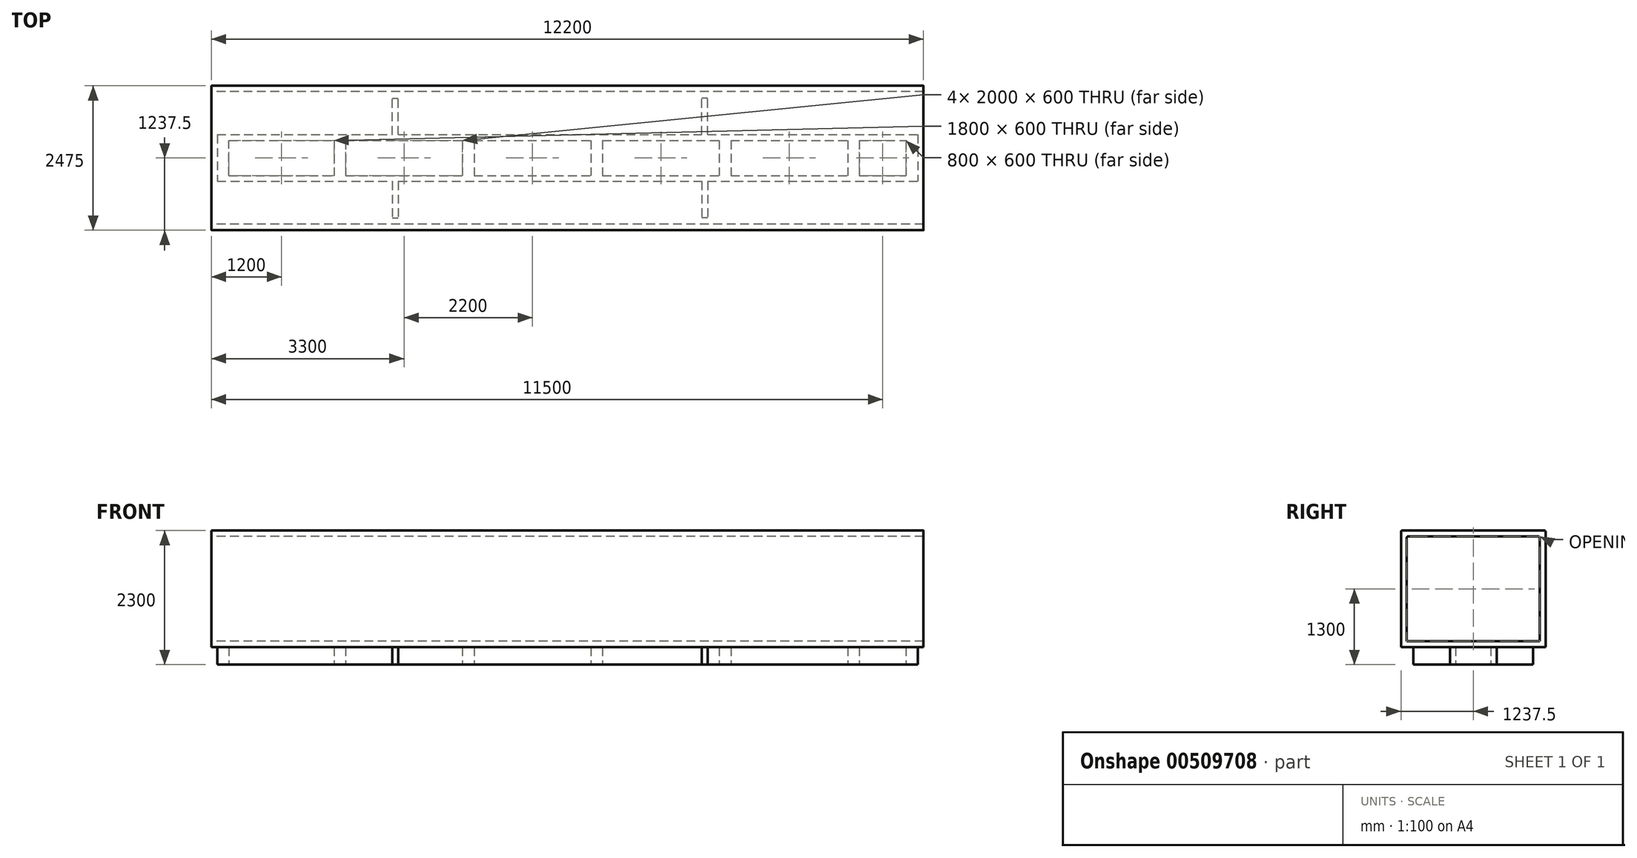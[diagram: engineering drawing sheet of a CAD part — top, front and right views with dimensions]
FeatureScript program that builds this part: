
annotation { "Feature Type Name" : "Feature", "Feature Type Description" : "" }
export const myFeature = defineFeature(function(context is Context, id is Id, definition is map)
    precondition{}
    {
        {
            var Q0;
            Q0=qCreatedBy(makeId("Top.planeOp"),FACE);
            var sketch = newSketch(context, id + "F0", { "sketchPlane" : qUnion([Q0])});
            skLineSegment(sketch, "E0.bottom", {"start": v(-69.8, 600) * mm, "end": v(11930.2, 600) * mm});
            skLineSegment(sketch, "E0.top", {"start": v(-69.8, 0) * mm, "end": v(11930.2, 0) * mm});
            skLineSegment(sketch, "E0.left", {"start": v(-69.8, 600) * mm, "end": v(-69.8, 0) * mm});
            skLineSegment(sketch, "E0.right", {"start": v(11930.2, 600) * mm, "end": v(11930.2, 0) * mm});
            skLineSegment(sketch, "E1.bottom", {"start": v(1930.2, 600) * mm, "end": v(2130.2, 600) * mm});
            skLineSegment(sketch, "E1.top", {"start": v(1930.2, 0) * mm, "end": v(2130.2, 0) * mm});
            skLineSegment(sketch, "E1.left", {"start": v(1930.2, 600) * mm, "end": v(1930.2, 0) * mm});
            skLineSegment(sketch, "E1.right", {"start": v(2130.2, 600) * mm, "end": v(2130.2, 0) * mm});
            skLineSegment(sketch, "E2.bottom", {"start": v(4130.2, 600) * mm, "end": v(4330.2, 600) * mm});
            skLineSegment(sketch, "E2.top", {"start": v(4130.2, 0) * mm, "end": v(4330.2, 0) * mm});
            skLineSegment(sketch, "E2.left", {"start": v(4130.2, 600) * mm, "end": v(4130.2, 0) * mm});
            skLineSegment(sketch, "E2.right", {"start": v(4330.2, 600) * mm, "end": v(4330.2, 0) * mm});
            skLineSegment(sketch, "E3.bottom", {"start": v(6330.2, 600) * mm, "end": v(6530.2, 600) * mm});
            skLineSegment(sketch, "E3.top", {"start": v(6330.2, 0) * mm, "end": v(6530.2, 0) * mm});
            skLineSegment(sketch, "E3.left", {"start": v(6330.2, 600) * mm, "end": v(6330.2, 0) * mm});
            skLineSegment(sketch, "E3.right", {"start": v(6530.2, 600) * mm, "end": v(6530.2, 0) * mm});
            skLineSegment(sketch, "E4.bottom", {"start": v(8530.2, 600) * mm, "end": v(8730.2, 600) * mm});
            skLineSegment(sketch, "E4.top", {"start": v(8530.2, 0) * mm, "end": v(8730.2, 0) * mm});
            skLineSegment(sketch, "E4.left", {"start": v(8530.2, 600) * mm, "end": v(8530.2, 0) * mm});
            skLineSegment(sketch, "E4.right", {"start": v(8730.2, 600) * mm, "end": v(8730.2, 0) * mm});
            skLineSegment(sketch, "E5.bottom", {"start": v(10730.2, 600) * mm, "end": v(10930.2, 600) * mm});
            skLineSegment(sketch, "E5.top", {"start": v(10730.2, 0) * mm, "end": v(10930.2, 0) * mm});
            skLineSegment(sketch, "E5.left", {"start": v(10730.2, 600) * mm, "end": v(10730.2, 0) * mm});
            skLineSegment(sketch, "E5.right", {"start": v(10930.2, 600) * mm, "end": v(10930.2, 0) * mm});
            skLineSegment(sketch, "E6", {"start": v(130.2, 0) * mm, "end": v(130.2, 600) * mm});
            skLineSegment(sketch, "E7", {"start": v(11730.2, 600) * mm, "end": v(11730.2, 0) * mm});
            skLineSegment(sketch, "E8.top", {"start": v(-69.8, 700) * mm, "end": v(11930.2, 700) * mm});
            skLineSegment(sketch, "E8.left", {"start": v(-69.8, 600) * mm, "end": v(-69.8, 700) * mm});
            skLineSegment(sketch, "E8.right", {"start": v(11930.2, 600) * mm, "end": v(11930.2, 700) * mm});
            skLineSegment(sketch, "E9.top", {"start": v(-69.8, -100) * mm, "end": v(11930.2, -100) * mm});
            skLineSegment(sketch, "E9.left", {"start": v(-69.8, 0) * mm, "end": v(-69.8, -100) * mm});
            skLineSegment(sketch, "E9.right", {"start": v(11930.2, 0) * mm, "end": v(11930.2, -100) * mm});
            skSolve(sketch);
        }
        {
            var Q0;
            {var subQ0=sQuery(id+"F0.wireOp",EDGE,"E0.left");Q0=makeQuery(id+"F0.imprint","IMPRINT",FACE,{"disambiguationData":[TD([[makeQuery(id+"F0.imprint","IMPRINT",EDGE,{"derivedFrom":subQ0}),1.0]])]});}
            var Q1;
            {var subQ0=sQuery(id+"F0.wireOp",EDGE,"E1.left");Q1=makeQuery(id+"F0.imprint","IMPRINT",FACE,{"disambiguationData":[TD([[makeQuery(id+"F0.imprint","IMPRINT",EDGE,{"derivedFrom":subQ0}),1.0]])]});}
            var Q2;
            Q2=makeQuery(id+"F0.imprint","IMPRINT",FACE,{"disambiguationData":[TD([[makeQuery(id+"F0.imprint","IMPRINT",EDGE,{"derivedFrom":sQuery(id+"F0.wireOp",EDGE,"E9.top")}),1.0]])]});
            var Q3;
            Q3=makeQuery(id+"F0.imprint","IMPRINT",FACE,{"disambiguationData":[TD([[makeQuery(id+"F0.imprint","IMPRINT",EDGE,{"derivedFrom":sQuery(id+"F0.wireOp",EDGE,"E8.top")}),-1.0]])]});
            var Q4;
            {var subQ0=sQuery(id+"F0.wireOp",EDGE,"E2.left");Q4=makeQuery(id+"F0.imprint","IMPRINT",FACE,{"disambiguationData":[TD([[makeQuery(id+"F0.imprint","IMPRINT",EDGE,{"derivedFrom":subQ0}),1.0]])]});}
            var Q5;
            {var subQ0=sQuery(id+"F0.wireOp",EDGE,"E3.left");Q5=makeQuery(id+"F0.imprint","IMPRINT",FACE,{"disambiguationData":[TD([[makeQuery(id+"F0.imprint","IMPRINT",EDGE,{"derivedFrom":subQ0}),1.0]])]});}
            var Q6;
            {var subQ0=sQuery(id+"F0.wireOp",EDGE,"E4.left");Q6=makeQuery(id+"F0.imprint","IMPRINT",FACE,{"disambiguationData":[TD([[makeQuery(id+"F0.imprint","IMPRINT",EDGE,{"derivedFrom":subQ0}),1.0]])]});}
            var Q7;
            {var subQ0=sQuery(id+"F0.wireOp",EDGE,"E5.left");Q7=makeQuery(id+"F0.imprint","IMPRINT",FACE,{"disambiguationData":[TD([[makeQuery(id+"F0.imprint","IMPRINT",EDGE,{"derivedFrom":subQ0}),1.0]])]});}
            var Q8;
            {var subQ0=sQuery(id+"F0.wireOp",EDGE,"E0.right");Q8=makeQuery(id+"F0.imprint","IMPRINT",FACE,{"disambiguationData":[TD([[makeQuery(id+"F0.imprint","IMPRINT",EDGE,{"derivedFrom":subQ0}),-1.0]])]});}
            extrude(context, id + "F1", {"entities" : qUnion([Q0, Q1, Q2, Q3, Q4, Q5, Q6, Q7, Q8]), "depth" : 300 * mm});
        }
        {
            var Q0;
            Q0=makeQuery(id+"F1.opExtrude","CAP_FACE",FACE,{"disambiguationData":[OSD([sQuery(id+"F0.wireOp",EDGE,"E0.left"),sQuery(id+"F0.wireOp",EDGE,"E0.right"),sQuery(id+"F0.wireOp",EDGE,"E1.left"),sQuery(id+"F0.wireOp",EDGE,"E1.right"),sQuery(id+"F0.wireOp",EDGE,"E2.left"),sQuery(id+"F0.wireOp",EDGE,"E2.right"),sQuery(id+"F0.wireOp",EDGE,"E3.left"),sQuery(id+"F0.wireOp",EDGE,"E3.right"),sQuery(id+"F0.wireOp",EDGE,"E4.left"),sQuery(id+"F0.wireOp",EDGE,"E4.right"),sQuery(id+"F0.wireOp",EDGE,"E5.left"),sQuery(id+"F0.wireOp",EDGE,"E5.right"),sQuery(id+"F0.wireOp",EDGE,"E6"),sQuery(id+"F0.wireOp",EDGE,"E7"),sQuery(id+"F0.wireOp",EDGE,"E0.bottom"),sQuery(id+"F0.wireOp",EDGE,"E8.top"),sQuery(id+"F0.wireOp",EDGE,"E8.left"),sQuery(id+"F0.wireOp",EDGE,"E8.right"),sQuery(id+"F0.wireOp",EDGE,"E0.top"),sQuery(id+"F0.wireOp",EDGE,"E9.top"),sQuery(id+"F0.wireOp",EDGE,"E9.left"),sQuery(id+"F0.wireOp",EDGE,"E9.right")])],"isStart":false});
            var sketch = newSketch(context, id + "F2", { "sketchPlane" : qUnion([Q0])});
            skLineSegment(sketch, "E10.bottom", {"start": v(2930.2, 700) * mm, "end": v(3030.2, 700) * mm});
            skLineSegment(sketch, "E10.top", {"start": v(2930.2, 1327) * mm, "end": v(3030.2, 1327) * mm});
            skLineSegment(sketch, "E10.left", {"start": v(3030.2, 700) * mm, "end": v(3030.2, 1327) * mm});
            skLineSegment(sketch, "E10.right", {"start": v(2930.2, 700) * mm, "end": v(2930.2, 1327) * mm});
            skLineSegment(sketch, "E11.bottom", {"start": v(2930.2, -100) * mm, "end": v(3030.2, -100) * mm});
            skLineSegment(sketch, "E11.top", {"start": v(2930.2, -727) * mm, "end": v(3030.2, -727) * mm});
            skLineSegment(sketch, "E11.left", {"start": v(2930.2, -100) * mm, "end": v(2930.2, -727) * mm});
            skLineSegment(sketch, "E11.right", {"start": v(3030.2, -100) * mm, "end": v(3030.2, -727) * mm});
            skLineSegment(sketch, "E12.bottom", {"start": v(8330.2, 700) * mm, "end": v(8230.2, 700) * mm});
            skLineSegment(sketch, "E12.top", {"start": v(8330.2, 1327) * mm, "end": v(8230.2, 1327) * mm});
            skLineSegment(sketch, "E12.left", {"start": v(8330.2, 700) * mm, "end": v(8330.2, 1327) * mm});
            skLineSegment(sketch, "E12.right", {"start": v(8230.2, 700) * mm, "end": v(8230.2, 1327) * mm});
            skLineSegment(sketch, "E13.bottom", {"start": v(8330.2, -100) * mm, "end": v(8230.2, -100) * mm});
            skLineSegment(sketch, "E13.top", {"start": v(8330.2, -727) * mm, "end": v(8230.2, -727) * mm});
            skLineSegment(sketch, "E13.left", {"start": v(8330.2, -100) * mm, "end": v(8330.2, -727) * mm});
            skLineSegment(sketch, "E13.right", {"start": v(8230.2, -100) * mm, "end": v(8230.2, -727) * mm});
            skSolve(sketch);
        }
        {
            var Q0;
            Q0=makeQuery(id+"F2.imprint","IMPRINT",FACE,{"disambiguationData":[TD([[makeQuery(id+"F2.imprint","IMPRINT",EDGE,{"derivedFrom":sQuery(id+"F2.wireOp",EDGE,"E11.bottom")}),-1.0]])]});
            var Q1;
            Q1=makeQuery(id+"F2.imprint","IMPRINT",FACE,{"disambiguationData":[TD([[makeQuery(id+"F2.imprint","IMPRINT",EDGE,{"derivedFrom":sQuery(id+"F2.wireOp",EDGE,"E10.bottom")}),1.0]])]});
            var Q2;
            Q2=makeQuery(id+"F2.imprint","IMPRINT",FACE,{"disambiguationData":[TD([[makeQuery(id+"F2.imprint","IMPRINT",EDGE,{"derivedFrom":sQuery(id+"F2.wireOp",EDGE,"E13.bottom")}),-1.0]])]});
            var Q3;
            Q3=makeQuery(id+"F2.imprint","IMPRINT",FACE,{"disambiguationData":[TD([[makeQuery(id+"F2.imprint","IMPRINT",EDGE,{"derivedFrom":sQuery(id+"F2.wireOp",EDGE,"E12.bottom")}),1.0]])]});
            extrude(context, id + "F3", {"entities" : qUnion([Q0, Q1, Q2, Q3]), "operationType" : NewBodyOperationType.ADD, "oppositeDirection" : true, "depth" : 300 * mm});
        }
        {
            var Q0;
            Q0=makeQuery(id+"F3.boolean.opBoolean","MERGE",FACE,{"derivedFrom":[makeQuery(id+"F1.opExtrude","CAP_FACE",FACE,{"disambiguationData":[OSD([sQuery(id+"F0.wireOp",EDGE,"E0.left"),sQuery(id+"F0.wireOp",EDGE,"E0.right"),sQuery(id+"F0.wireOp",EDGE,"E1.left"),sQuery(id+"F0.wireOp",EDGE,"E1.right"),sQuery(id+"F0.wireOp",EDGE,"E2.left"),sQuery(id+"F0.wireOp",EDGE,"E2.right"),sQuery(id+"F0.wireOp",EDGE,"E3.left"),sQuery(id+"F0.wireOp",EDGE,"E3.right"),sQuery(id+"F0.wireOp",EDGE,"E4.left"),sQuery(id+"F0.wireOp",EDGE,"E4.right"),sQuery(id+"F0.wireOp",EDGE,"E5.left"),sQuery(id+"F0.wireOp",EDGE,"E5.right"),sQuery(id+"F0.wireOp",EDGE,"E6"),sQuery(id+"F0.wireOp",EDGE,"E7"),sQuery(id+"F0.wireOp",EDGE,"E0.bottom"),sQuery(id+"F0.wireOp",EDGE,"E8.top"),sQuery(id+"F0.wireOp",EDGE,"E8.left"),sQuery(id+"F0.wireOp",EDGE,"E8.right"),sQuery(id+"F0.wireOp",EDGE,"E0.top"),sQuery(id+"F0.wireOp",EDGE,"E9.top"),sQuery(id+"F0.wireOp",EDGE,"E9.left"),sQuery(id+"F0.wireOp",EDGE,"E9.right")])],"isStart":false}),makeQuery(id+"F3.opExtrude","CAP_FACE",FACE,{"disambiguationData":[OSD([sQuery(id+"F2.wireOp",EDGE,"E10.bottom"),sQuery(id+"F2.wireOp",EDGE,"E10.top"),sQuery(id+"F2.wireOp",EDGE,"E10.left"),sQuery(id+"F2.wireOp",EDGE,"E10.right")])],"isStart":true}),makeQuery(id+"F3.opExtrude","CAP_FACE",FACE,{"disambiguationData":[OSD([sQuery(id+"F2.wireOp",EDGE,"E11.bottom"),sQuery(id+"F2.wireOp",EDGE,"E11.top"),sQuery(id+"F2.wireOp",EDGE,"E11.left"),sQuery(id+"F2.wireOp",EDGE,"E11.right")])],"isStart":true}),makeQuery(id+"F3.opExtrude","CAP_FACE",FACE,{"disambiguationData":[OSD([sQuery(id+"F2.wireOp",EDGE,"E12.bottom"),sQuery(id+"F2.wireOp",EDGE,"E12.top"),sQuery(id+"F2.wireOp",EDGE,"E12.left"),sQuery(id+"F2.wireOp",EDGE,"E12.right")])],"isStart":true}),makeQuery(id+"F3.opExtrude","CAP_FACE",FACE,{"disambiguationData":[OSD([sQuery(id+"F2.wireOp",EDGE,"E13.bottom"),sQuery(id+"F2.wireOp",EDGE,"E13.top"),sQuery(id+"F2.wireOp",EDGE,"E13.left"),sQuery(id+"F2.wireOp",EDGE,"E13.right")])],"isStart":true})]});
            var sketch = newSketch(context, id + "F4", { "sketchPlane" : qUnion([Q0])});
            skLineSegment(sketch, "E14.bottom", {"start": v(-169.8, 1537.5) * mm, "end": v(12030.2, 1537.5) * mm});
            skLineSegment(sketch, "E14.top", {"start": v(-169.8, -937.5) * mm, "end": v(12030.2, -937.5) * mm});
            skLineSegment(sketch, "E14.left", {"start": v(-169.8, 1537.5) * mm, "end": v(-169.8, -937.5) * mm});
            skLineSegment(sketch, "E14.right", {"start": v(12030.2, 1537.5) * mm, "end": v(12030.2, -937.5) * mm});
            skSolve(sketch);
        }
        {
            var Q0;
            Q0=makeQuery(id+"F4.imprint","IMPRINT",FACE,{"disambiguationData":[TD([[makeQuery(id+"F4.imprint","IMPRINT",EDGE,{"derivedFrom":sQuery(id+"F4.wireOp",EDGE,"E14.bottom")}),-1.0]])]});
            var Q1;
            {var subQ3=sQuery(id+"F0.wireOp",EDGE,"E1.left");Q1=makeQuery(id+"F4.imprint","IMPRINT",FACE,{"disambiguationData":[TD([[makeQuery(id+"F4.imprint","IMPRINT",EDGE,{"derivedFrom":makeQuery(id+"F1.opExtrude","CAP_EDGE",EDGE,{"disambiguationData":[OSD([subQ3])],"isStart":false})}),1.0]])]});}
            var Q2;
            {var subQ0=sQuery(id+"F0.wireOp",EDGE,"E2.right");Q2=makeQuery(id+"F4.imprint","IMPRINT",FACE,{"disambiguationData":[TD([[makeQuery(id+"F4.imprint","IMPRINT",EDGE,{"derivedFrom":makeQuery(id+"F1.opExtrude","CAP_EDGE",EDGE,{"disambiguationData":[OSD([subQ0])],"isStart":false})}),1.0]])]});}
            var Q3;
            {var subQ0=sQuery(id+"F0.wireOp",EDGE,"E1.right");Q3=makeQuery(id+"F4.imprint","IMPRINT",FACE,{"disambiguationData":[TD([[makeQuery(id+"F4.imprint","IMPRINT",EDGE,{"derivedFrom":makeQuery(id+"F1.opExtrude","CAP_EDGE",EDGE,{"disambiguationData":[OSD([subQ0])],"isStart":false})}),1.0]])]});}
            var Q4;
            {var subQ0=sQuery(id+"F0.wireOp",EDGE,"E3.right");Q4=makeQuery(id+"F4.imprint","IMPRINT",FACE,{"disambiguationData":[TD([[makeQuery(id+"F4.imprint","IMPRINT",EDGE,{"derivedFrom":makeQuery(id+"F1.opExtrude","CAP_EDGE",EDGE,{"disambiguationData":[OSD([subQ0])],"isStart":false})}),1.0]])]});}
            var Q5;
            {var subQ0=sQuery(id+"F0.wireOp",EDGE,"E1.left");Q5=makeQuery(id+"F4.imprint","IMPRINT",FACE,{"disambiguationData":[TD([[makeQuery(id+"F4.imprint","IMPRINT",EDGE,{"derivedFrom":makeQuery(id+"F1.opExtrude","CAP_EDGE",EDGE,{"disambiguationData":[OSD([subQ0])],"isStart":false})}),-1.0]])]});}
            var Q6;
            {var subQ0=sQuery(id+"F0.wireOp",EDGE,"E4.right");Q6=makeQuery(id+"F4.imprint","IMPRINT",FACE,{"disambiguationData":[TD([[makeQuery(id+"F4.imprint","IMPRINT",EDGE,{"derivedFrom":makeQuery(id+"F1.opExtrude","CAP_EDGE",EDGE,{"disambiguationData":[OSD([subQ0])],"isStart":false})}),1.0]])]});}
            var Q7;
            {var subQ0=sQuery(id+"F0.wireOp",EDGE,"E5.right");Q7=makeQuery(id+"F4.imprint","IMPRINT",FACE,{"disambiguationData":[TD([[makeQuery(id+"F4.imprint","IMPRINT",EDGE,{"derivedFrom":makeQuery(id+"F1.opExtrude","CAP_EDGE",EDGE,{"disambiguationData":[OSD([subQ0])],"isStart":false})}),1.0]])]});}
            extrude(context, id + "F5", {"entities" : qUnion([Q0, Q1, Q2, Q3, Q4, Q5, Q6, Q7]), "depth" : 2000 * mm});
        }
        {
            var Q0;
            Q0=makeQuery(id+"F5.opExtrude","CAP_EDGE",EDGE,{"disambiguationData":[OSD([sQuery(id+"F4.wireOp",EDGE,"E14.bottom")])],"isStart":false});
            var Q1;
            Q1=makeQuery(id+"F5.opExtrude","CAP_EDGE",EDGE,{"disambiguationData":[OSD([sQuery(id+"F4.wireOp",EDGE,"E14.top")])],"isStart":false});
            fillet(context, id + "F6", {"entities" : qUnion([Q0, Q1]), "radius" : 20 * mm, "tangentPropagation" : true, "allowEdgeOverflow" : false});
        }
        {
            var Q0;
            Q0=makeQuery(id+"F5.opExtrude","SWEPT_FACE",FACE,{"disambiguationData":[OSD([sQuery(id+"F4.wireOp",EDGE,"E14.left")])]});
            var sketch = newSketch(context, id + "F7", { "sketchPlane" : qUnion([Q0])});
            skLineSegment(sketch, "E15.bottom", {"start": v(-1437.5, 2200) * mm, "end": v(837.5, 2200) * mm});
            skLineSegment(sketch, "E15.top", {"start": v(-1437.5, 400) * mm, "end": v(837.5, 400) * mm});
            skLineSegment(sketch, "E15.left", {"start": v(-1437.5, 2200) * mm, "end": v(-1437.5, 400) * mm});
            skLineSegment(sketch, "E15.right", {"start": v(837.5, 2200) * mm, "end": v(837.5, 400) * mm});
            skSolve(sketch);
        }
        {
            var Q0;
            Q0=makeQuery(id+"F7.imprint","IMPRINT",FACE,{"disambiguationData":[TD([[makeQuery(id+"F7.imprint","IMPRINT",EDGE,{"derivedFrom":sQuery(id+"F7.wireOp",EDGE,"E15.bottom")}),-1.0]])]});
            extrude(context, id + "F8", {"entities" : qUnion([Q0]), "operationType" : NewBodyOperationType.REMOVE, "oppositeDirection" : true, "depth" : 12500 * mm});
        }
        {
            var Q0;
            Q0=makeQuery(id+"F8.boolean.opBoolean","COPY",EDGE,{"derivedFrom":makeQuery(id+"F8.opExtrude","SWEPT_EDGE",EDGE,{"disambiguationData":[OSD([sQuery(id+"F7.wireOp",EDGE,"E15.bottom"),sQuery(id+"F7.wireOp",EDGE,"E15.left")])]})});
            var Q1;
            Q1=makeQuery(id+"F8.boolean.opBoolean","COPY",EDGE,{"derivedFrom":makeQuery(id+"F8.opExtrude","SWEPT_EDGE",EDGE,{"disambiguationData":[OSD([sQuery(id+"F7.wireOp",EDGE,"E15.bottom"),sQuery(id+"F7.wireOp",EDGE,"E15.right")])]})});
            fillet(context, id + "F9", {"entities" : qUnion([Q0, Q1]), "radius" : 20 * mm, "tangentPropagation" : true, "allowEdgeOverflow" : false});
        }
    });
